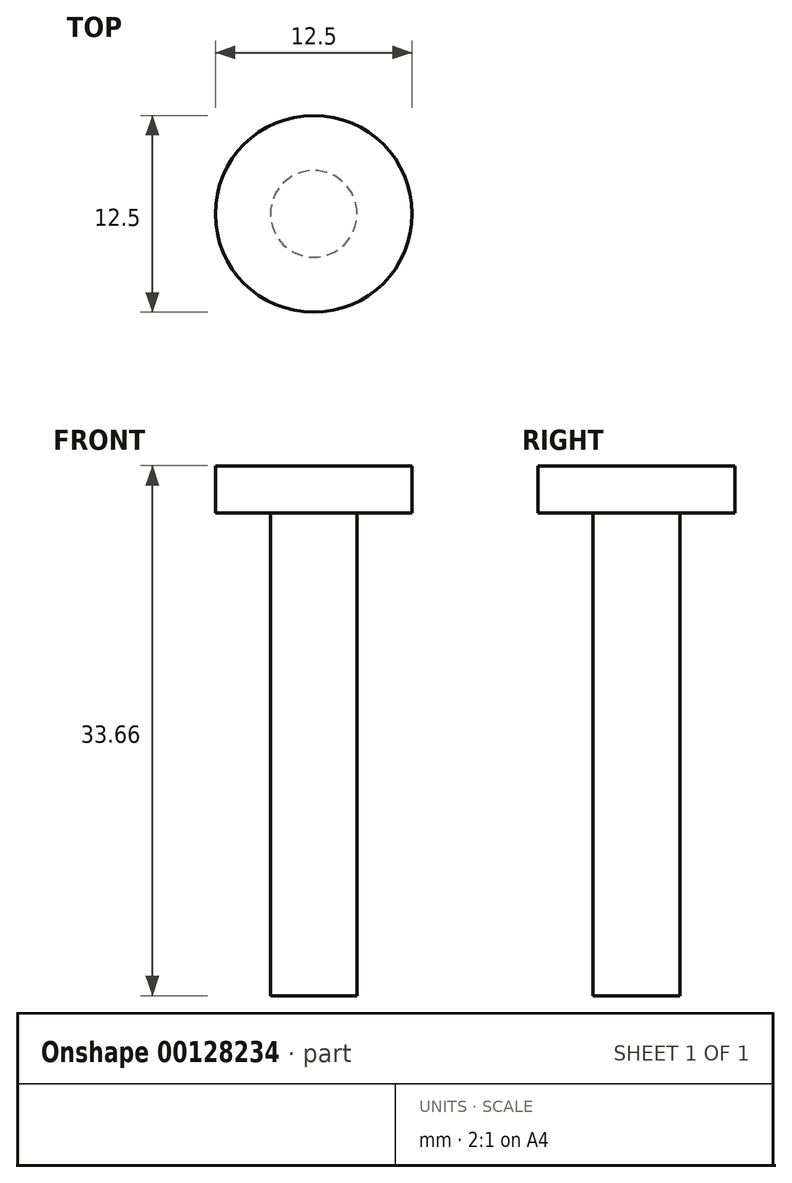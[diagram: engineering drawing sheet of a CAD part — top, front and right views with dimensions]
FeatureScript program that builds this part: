
annotation { "Feature Type Name" : "Feature", "Feature Type Description" : "" }
export const myFeature = defineFeature(function(context is Context, id is Id, definition is map)
    precondition{}
    {
        {
            var Q0;
            Q0=qCreatedBy(makeId("Top.planeOp"),FACE);
            var sketch = newSketch(context, id + "F0", { "sketchPlane" : qUnion([Q0])});
            skCircle(sketch, "E0", {"center": v(0, 0) * mm, "radius": 2.75 * mm});
            skSolve(sketch);
        }
        {
            var Q0;
            Q0=makeQuery(id+"F0.imprint","IMPRINT",FACE,{"disambiguationData":[TD([[makeQuery(id+"F0.imprint","IMPRINT",EDGE,{"derivedFrom":sQuery(id+"F0.wireOp",EDGE,"E0")}),1.0]])]});
            extrude(context, id + "F1", {"entities" : qUnion([Q0]), "depth" : 32.16 * mm});
        }
        {
            var Q0;
            Q0=makeQuery(id+"F1.opExtrude","CAP_FACE",FACE,{"disambiguationData":[OSD([sQuery(id+"F0.wireOp",EDGE,"E0")])],"isStart":false});
            var sketch = newSketch(context, id + "F2", { "sketchPlane" : qUnion([Q0])});
            skCircle(sketch, "E1", {"center": v(0, 0) * mm, "radius": 6.25 * mm});
            skSolve(sketch);
        }
        {
            var Q0;
            Q0=makeQuery(id+"F2.imprint","IMPRINT",FACE,{"disambiguationData":[TD([[makeQuery(id+"F2.imprint","IMPRINT",EDGE,{"derivedFrom":sQuery(id+"F2.wireOp",EDGE,"E1")}),1.0]])]});
            var Q1;
            Q1=makeQuery(id+"F2.imprint","IMPRINT",FACE,{"disambiguationData":[TD([[makeQuery(id+"F2.imprint","IMPRINT",EDGE,{"derivedFrom":makeQuery(id+"F1.opExtrude","CAP_EDGE",EDGE,{"disambiguationData":[OSD([sQuery(id+"F0.wireOp",EDGE,"E0")])],"isStart":true})}),-1.0]])]});
            var Q2;
            Q2=makeQuery(id+"F2.imprint","IMPRINT",FACE,{"disambiguationData":[TD([[makeQuery(id+"F2.imprint","IMPRINT",EDGE,{"derivedFrom":makeQuery(id+"F1.opExtrude","CAP_EDGE",EDGE,{"disambiguationData":[OSD([sQuery(id+"F0.wireOp",EDGE,"E0")])],"isStart":false})}),1.0]])]});
            extrude(context, id + "F3", {"entities" : qUnion([Q0, Q1, Q2]), "operationType" : NewBodyOperationType.ADD, "depth" : 1.5 * mm, "hasSecondDirection" : true, "secondDirectionOppositeDirection" : true, "secondDirectionDepth" : 1.5 * mm});
        }
    });
